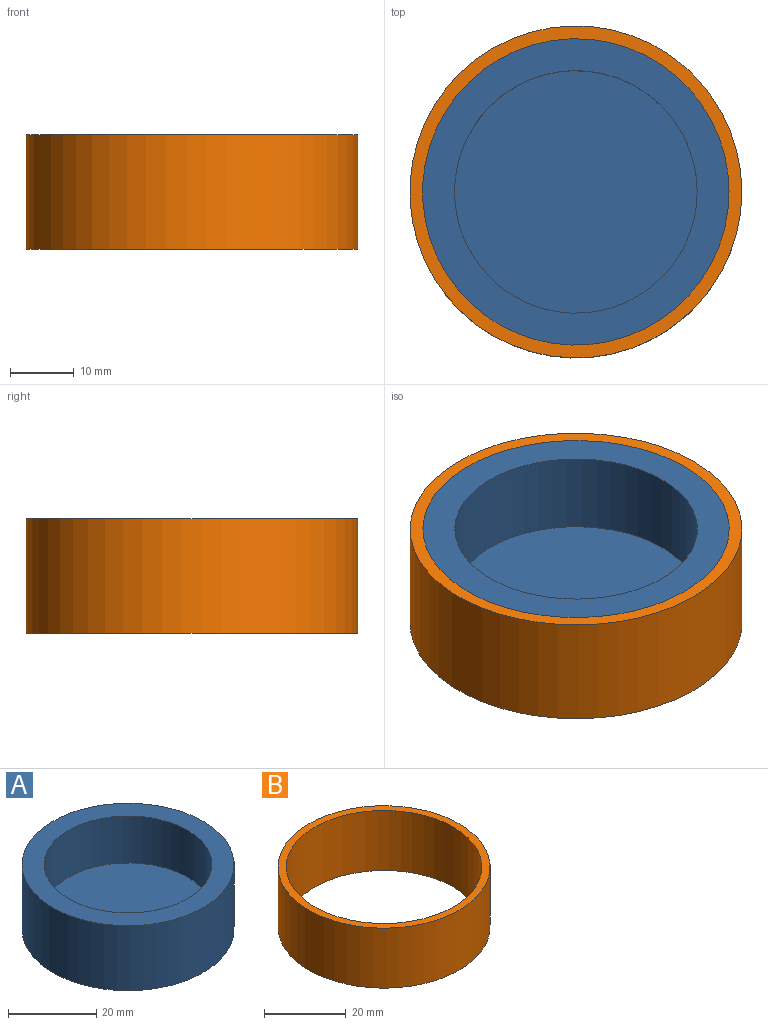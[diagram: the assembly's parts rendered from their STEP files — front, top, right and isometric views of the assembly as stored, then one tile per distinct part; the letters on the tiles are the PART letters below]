
ASSEMBLY  parts=2 mates=1
PART A: 5 faces, bbox 48x48x18 mm
  f0: plane 38x38mm, normal (0,0,1), area 1134.1mm2, adj f1
  f1: cylinder r=19mm len=38mm, axis (0,0,-1), area 1551.9mm2, adj f0,f3
  f2: cylinder r=24mm len=48mm, axis (0,0,-1), area 2714.3mm2, adj f3,f4
  f3: plane 48x48mm, normal (0,0,1), area 675.4mm2, adj f1,f2
  f4: plane 48x48mm, normal (0,0,-1), area 1809.6mm2, adj f2
PART B: 4 faces, bbox 52x52x18 mm
  f0: plane 52x52mm, normal (0,0,1), area 314.2mm2, adj f1,f2
  f1: cylinder r=24mm len=48mm, axis (0,0,-1), area 2714.3mm2, adj f0,f3
  f2: cylinder r=26mm len=52mm, axis (0,0,-1), area 2940.5mm2, adj f0,f3
  f3: plane 52x52mm, normal (0,0,-1), area 314.2mm2, adj f1,f2
PLACE A at identity
PLACE B at identity
MATE fastened A.f2 <-> B.f2  axis (0,0,-1) through (0,0,0)mm
